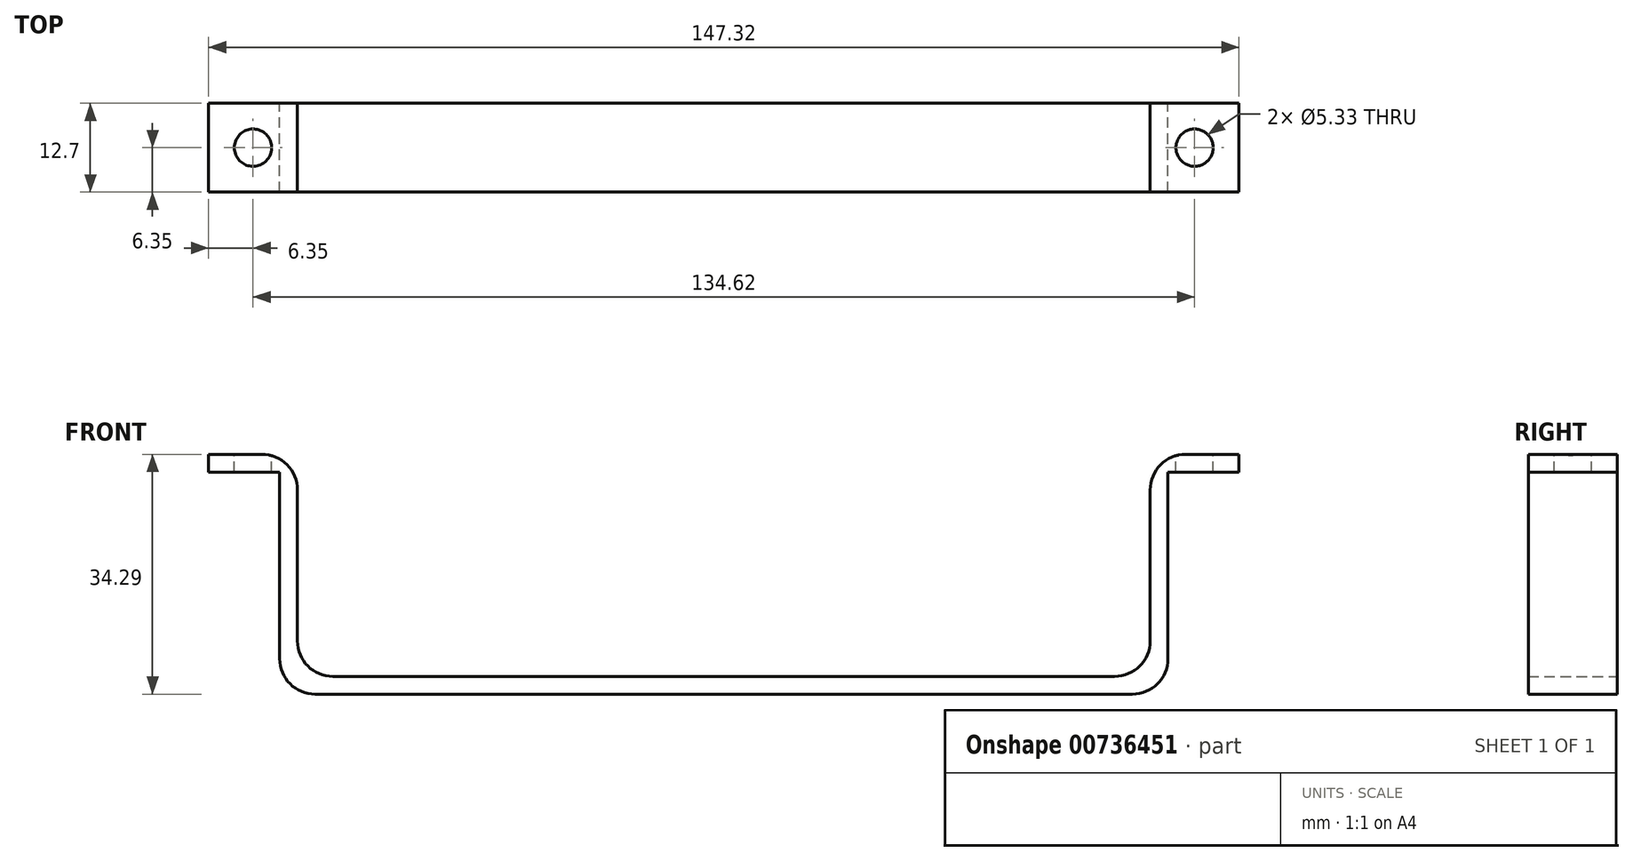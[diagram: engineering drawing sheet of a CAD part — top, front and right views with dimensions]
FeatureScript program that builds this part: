
annotation { "Feature Type Name" : "Feature", "Feature Type Description" : "" }
export const myFeature = defineFeature(function(context is Context, id is Id, definition is map)
    precondition{}
    {
        {
            var Q0;
            Q0=qCreatedBy(makeId("Front.planeOp"),FACE);
            var sketch = newSketch(context, id + "F0", { "sketchPlane" : qUnion([Q0])});
            skLineSegment(sketch, "E0", {"start": v(0, 0) * mm, "end": v(121.92, 0) * mm});
            skLineSegment(sketch, "E1", {"start": v(121.92, 0) * mm, "end": v(121.92, 31.75) * mm});
            skLineSegment(sketch, "E2", {"start": v(0, 0) * mm, "end": v(0, 31.75) * mm});
            skLineSegment(sketch, "E3", {"start": v(0, 31.75) * mm, "end": v(-12.7, 31.75) * mm});
            skLineSegment(sketch, "E4", {"start": v(121.92, 31.75) * mm, "end": v(134.62, 31.75) * mm});
            skLineSegment(sketch, "E5.0", {"start": v(124.46, 29.2) * mm, "end": v(134.62, 29.2) * mm});
            skLineSegment(sketch, "E5.1", {"start": v(-2.54, 29.2) * mm, "end": v(-12.7, 29.2) * mm});
            skLineSegment(sketch, "E5.2", {"start": v(-2.54, -2.54) * mm, "end": v(-2.54, 29.2) * mm});
            skLineSegment(sketch, "E5.3", {"start": v(-2.54, -2.54) * mm, "end": v(124.46, -2.54) * mm});
            skLineSegment(sketch, "E5.4", {"start": v(124.46, -2.54) * mm, "end": v(124.46, 29.2) * mm});
            skLineSegment(sketch, "E6", {"start": v(-12.7, 31.75) * mm, "end": v(-12.7, 29.2) * mm});
            skLineSegment(sketch, "E7", {"start": v(134.62, 31.75) * mm, "end": v(134.62, 29.2) * mm});
            skSolve(sketch);
        }
        {
            var Q0;
            Q0=makeQuery(id+"F0.imprint","IMPRINT",FACE,{"disambiguationData":[TD([[makeQuery(id+"F0.imprint","IMPRINT",EDGE,{"derivedFrom":sQuery(id+"F0.wireOp",EDGE,"E0")}),-1.0]])]});
            extrude(context, id + "F1", {"entities" : qUnion([Q0]), "depth" : 12.7 * mm, "offsetDistance" : 25.4 * mm});
        }
        {
            var Q0;
            Q0=makeQuery(id+"F1.opExtrude","SWEPT_FACE",FACE,{"disambiguationData":[OSD([sQuery(id+"F0.wireOp",EDGE,"E3")])]});
            var sketch = newSketch(context, id + "F2", { "sketchPlane" : qUnion([Q0])});
            skLineSegment(sketch, "E8", {"start": v(-12.7, 0) * mm, "end": v(-12.7, -6.35) * mm, "construction": true});
            skLineSegment(sketch, "E9", {"start": v(-12.7, -6.35) * mm, "end": v(0, -6.35) * mm, "construction": true});
            skLineSegment(sketch, "E10", {"start": v(0, -6.35) * mm, "end": v(0, 0) * mm, "construction": true});
            skLineSegment(sketch, "E11", {"start": v(0, 0) * mm, "end": v(-6.35, 0) * mm, "construction": true});
            skLineSegment(sketch, "E12", {"start": v(-6.35, 0) * mm, "end": v(-6.35, -12.7) * mm, "construction": true});
            skCircle(sketch, "E13", {"center": v(-6.35, -6.35) * mm, "radius": 2.67 * mm});
            skSolve(sketch);
        }
        {
            var Q0;
            Q0=makeQuery(id+"F1.opExtrude","SWEPT_FACE",FACE,{"disambiguationData":[OSD([sQuery(id+"F0.wireOp",EDGE,"E4")])]});
            var sketch = newSketch(context, id + "F3", { "sketchPlane" : qUnion([Q0])});
            skLineSegment(sketch, "E14", {"start": v(121.92, 0) * mm, "end": v(128.27, 0) * mm, "construction": true});
            skLineSegment(sketch, "E15", {"start": v(128.27, -12.7) * mm, "end": v(128.27, 0) * mm, "construction": true});
            skLineSegment(sketch, "E16", {"start": v(134.62, -6.35) * mm, "end": v(121.92, -6.35) * mm, "construction": true});
            skLineSegment(sketch, "E17", {"start": v(121.92, -6.35) * mm, "end": v(121.92, 0) * mm, "construction": true});
            skCircle(sketch, "E18", {"center": v(128.27, -6.35) * mm, "radius": 2.67 * mm});
            skPoint(sketch, "E18.perimeterSnap0", {"position": v(128.27, -6.35) * mm});
            skPoint(sketch, "E18.perimeterSnap1", {"position": v(121.92, -3.18) * mm});
            skSolve(sketch);
        }
        {
            var Q0;
            Q0=makeQuery(id+"F2.imprint","IMPRINT",FACE,{"disambiguationData":[TD([[makeQuery(id+"F2.imprint","IMPRINT",EDGE,{"derivedFrom":sQuery(id+"F2.wireOp",EDGE,"E13")}),1.0]])]});
            var Q1;
            Q1=makeQuery(id+"F3.imprint","IMPRINT",FACE,{"disambiguationData":[TD([[makeQuery(id+"F3.imprint","IMPRINT",EDGE,{"derivedFrom":sQuery(id+"F3.wireOp",EDGE,"E18")}),1.0]])]});
            extrude(context, id + "F4", {"entities" : qUnion([Q0, Q1]), "operationType" : NewBodyOperationType.REMOVE, "oppositeDirection" : true, "depth" : 25.4 * mm, "offsetDistance" : 25.4 * mm});
        }
        {
            var Q0;
            Q0=makeQuery(id+"F1.opExtrude","SWEPT_EDGE",EDGE,{"disambiguationData":[OSD([sQuery(id+"F0.wireOp",EDGE,"E5.2"),sQuery(id+"F0.wireOp",EDGE,"E5.3")])]});
            var Q1;
            Q1=makeQuery(id+"F1.opExtrude","SWEPT_EDGE",EDGE,{"disambiguationData":[OSD([sQuery(id+"F0.wireOp",EDGE,"E5.3"),sQuery(id+"F0.wireOp",EDGE,"E5.4")])]});
            var Q2;
            Q2=makeQuery(id+"F1.opExtrude","SWEPT_EDGE",EDGE,{"disambiguationData":[OSD([sQuery(id+"F0.wireOp",EDGE,"E0"),sQuery(id+"F0.wireOp",EDGE,"E2")])]});
            var Q3;
            Q3=makeQuery(id+"F1.opExtrude","SWEPT_EDGE",EDGE,{"disambiguationData":[OSD([sQuery(id+"F0.wireOp",EDGE,"E0"),sQuery(id+"F0.wireOp",EDGE,"E1")])]});
            var Q4;
            Q4=makeQuery(id+"F1.opExtrude","SWEPT_EDGE",EDGE,{"disambiguationData":[OSD([sQuery(id+"F0.wireOp",EDGE,"E1"),sQuery(id+"F0.wireOp",EDGE,"E4")])]});
            var Q5;
            Q5=makeQuery(id+"F1.opExtrude","SWEPT_EDGE",EDGE,{"disambiguationData":[OSD([sQuery(id+"F0.wireOp",EDGE,"E2"),sQuery(id+"F0.wireOp",EDGE,"E3")])]});
            fillet(context, id + "F5", {"entities" : qUnion([Q0, Q1, Q2, Q3, Q4, Q5]), "radius" : 5.08 * mm, "tangentPropagation" : true, "allowEdgeOverflow" : false});
        }
    });
